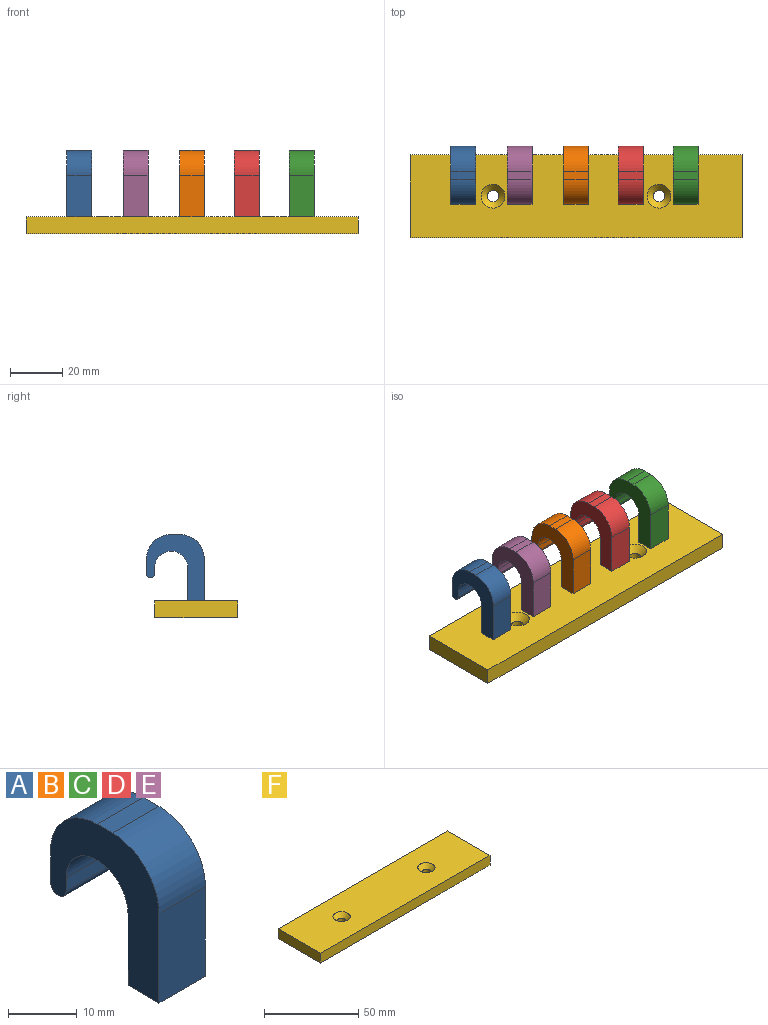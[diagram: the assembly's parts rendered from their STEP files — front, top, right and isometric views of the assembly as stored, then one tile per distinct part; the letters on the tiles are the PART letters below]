
ASSEMBLY  parts=6 mates=1
PART A: 12 faces, bbox 9.5x22.2x25.4 mm
  f0: cylinder r=6.35mm len=12.7mm, axis (-1,0,0), area 190mm2, adj f1,f9,f10,f11
  f1: plane 9.53x2.35mm, normal (0,-1,0), area 22.4mm2, adj f0,f2,f10,f11
  f2: cylinder r=1.59mm len=9.53mm, axis (-1,0,0), area 47.5mm2, adj f1,f3,f10,f11
  f3: plane 9.53x5.52mm, normal (0,1,0), area 52.6mm2, adj f2,f4,f10,f11
  f4: cylinder r=9.53mm len=9.53mm, axis (-1,0,0), area 142.5mm2, adj f3,f5,f10,f11
  f5: plane 9.53x3.18mm, normal (0,0,1), area 30.2mm2, adj f4,f6,f10,f11
  f6: cylinder r=9.53mm len=9.53mm, axis (-1,0,0), area 142.5mm2, adj f5,f7,f10,f11
  f7: plane 15.88x9.53mm, normal (0,-1,0), area 151.2mm2, adj f6,f8,f10,f11
  f8: plane 9.53x6.35mm, normal (0,0,-1), area 60.5mm2, adj f7,f9,f10,f11
  f9: plane 12.7x9.53mm, normal (0,1,0), area 121mm2, adj f0,f8,f10,f11
  f10: plane 25.4x22.23mm, normal (1,0,0), area 272mm2, adj f0,f1,f2,f3,f4,f5,f6,f7
  f11: plane 25.4x22.23mm, normal (-1,0,0), area 272mm2, adj f0,f1,f2,f3,f4,f5,f6,f7
PART B: same geometry as A
PART C: same geometry as A
PART D: same geometry as A
PART E: same geometry as A
PART F: 10 faces, bbox 127x31.8x6.4 mm
  f0: plane 31.75x6.35mm, normal (1,0,0), area 201.6mm2, adj f1,f3,f4,f5
  f1: plane 127x6.35mm, normal (0,1,0), area 806.5mm2, adj f0,f2,f4,f5
  f2: plane 31.75x6.35mm, normal (-1,0,0), area 201.6mm2, adj f1,f3,f4,f5
  f3: plane 127x6.35mm, normal (0,-1,0), area 806.5mm2, adj f0,f2,f4,f5
  f4: plane 127x31.75mm, normal (0,0,-1), area 4000.5mm2, adj f0,f1,f2,f3,f6,f8
  f5: plane 127x31.75mm, normal (0,0,1), area 3901.6mm2, adj f0,f1,f2,f3,f7,f9
  f6: cylinder r=2.25mm len=4.5mm, axis (0,0,1), area 52.1mm2, adj f4,f7
  f7: cone r=2.25mm half-angle=41deg, axis (0,0,1), area 75.3mm2, adj f5,f6
  f8: cylinder r=2.25mm len=4.5mm, axis (0,0,1), area 52.1mm2, adj f4,f9
  f9: cone r=2.25mm half-angle=41deg, axis (0,0,1), area 75.3mm2, adj f5,f8
PLACE A t=(-144.21,-46,18.34)mm
PLACE B t=(-101.03,-46,18.34)mm
PLACE C t=(-59.12,-46,18.34)mm
PLACE D t=(-80.08,-46,18.34)mm
PLACE E t=(-122.62,-46,18.34)mm
PLACE F t=(-32.77,-26.95,18.34)mm
MATE planar F.f5 <-> B.f8  axis (0,0,1) through (-96.27,-42.82,18.34)mm
